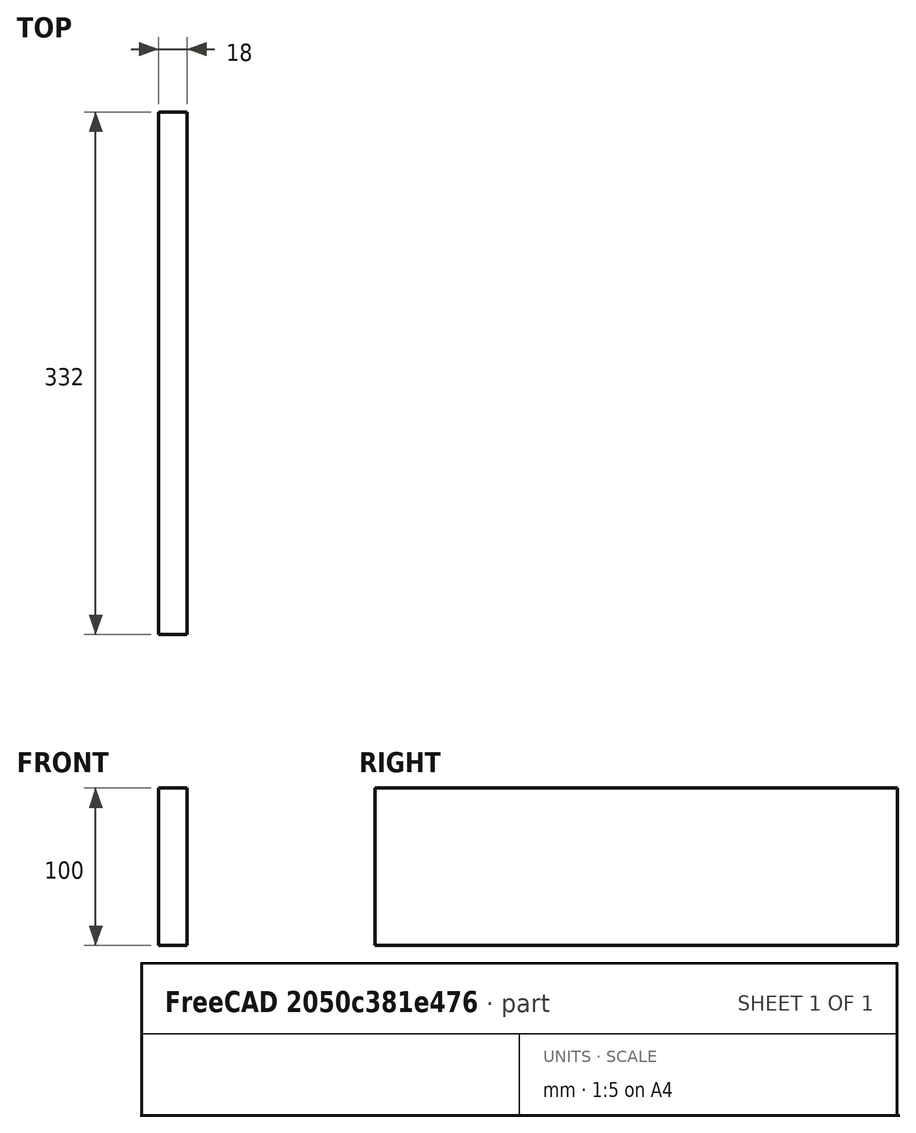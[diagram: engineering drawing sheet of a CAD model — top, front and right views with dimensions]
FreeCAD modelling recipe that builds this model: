
FCSTD DOCUMENT  (FreeCAD 0.18R4 (GitTag))
Label: drawer_side
License: All rights reserved
LicenseURL: http://en.wikipedia.org/wiki/All_rights_reserved
objects: Sketcher::SketchObject×1, PartDesign::Pad×1, PartDesign::Body×1
note: 4 computed .brp shape members not serialized (recipe doc carries the construction recipe); baked Part::Feature solids carry a one-line shape summary decoded from their .brp

FEATURE [Sketcher::SketchObject] Sketch
  MapMode = 5
  Placement = pos=(0,0,0) rot=(0.57735,0.57735,0.57735;2.0944rad)
  Support = -> [YZ_Plane]
  sketch-geometry (4):
    g0: LineSegment StartX=0 StartY=0 StartZ=0 EndX=-332 EndY=0 EndZ=0
    g1: LineSegment StartX=-332 StartY=0 StartZ=0 EndX=-332 EndY=100 EndZ=0
    g2: LineSegment StartX=-332 StartY=100 StartZ=0 EndX=0 EndY=100 EndZ=0
    g3: LineSegment StartX=0 StartY=100 StartZ=0 EndX=0 EndY=0 EndZ=0
  constraints (11):
    c: Coincident(g0,g1)
    c: Coincident(g1,g2)
    c: Coincident(g2,g3)
    c: Coincident(g3,g0)
    c: Horizontal(g0)
    c: Horizontal(g2)
    c: Vertical(g1)
    c: Vertical(g3)
    c: Coincident(g0,g-1)
    c: DistanceX(g0,g0) = 332
    c: DistanceY(g3,g3) = 100
FEATURE [PartDesign::Pad] Pad
  Length = 18
  Length2 = 100
  Placement = pos=(0,0,0) rot=(0.57735,0.57735,0.57735;2.0944rad)
  Profile = -> Sketch
  Type = 0
FEATURE [PartDesign::Body] Body
  Group = -> [Sketch,Pad]
  Origin = -> Origin
  Tip = -> Pad
